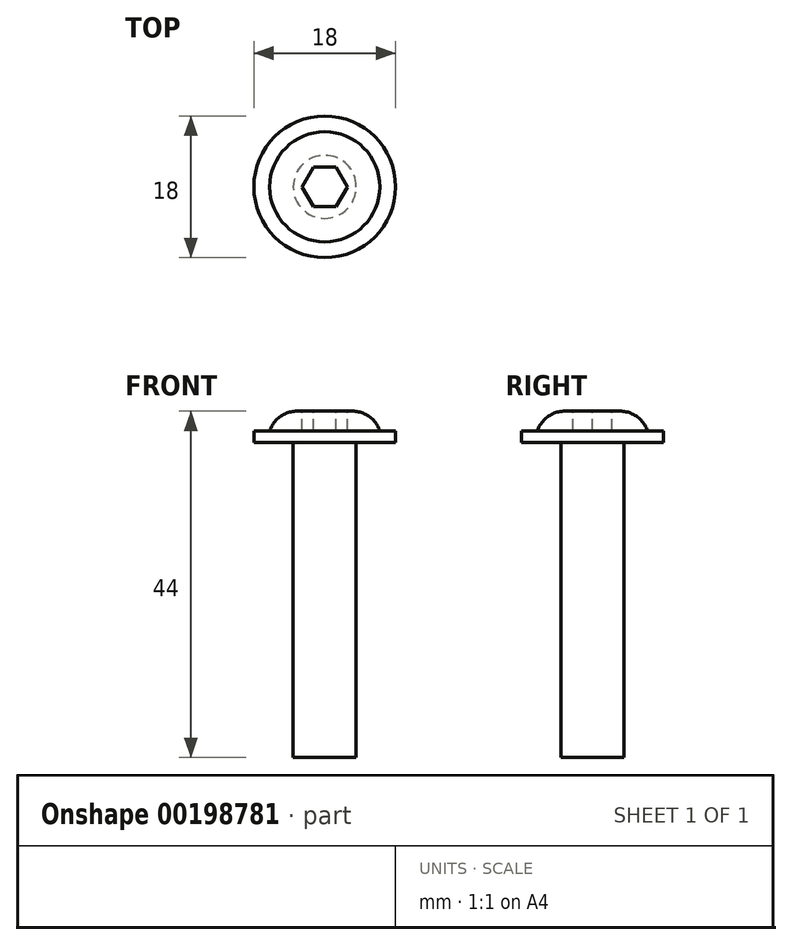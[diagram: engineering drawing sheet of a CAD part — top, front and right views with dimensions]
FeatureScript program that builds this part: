
annotation { "Feature Type Name" : "Feature", "Feature Type Description" : "" }
export const myFeature = defineFeature(function(context is Context, id is Id, definition is map)
    precondition{}
    {
        {
            var Q0;
            Q0=qCreatedBy(makeId("Front.planeOp"),FACE);
            var sketch = newSketch(context, id + "F0", { "sketchPlane" : qUnion([Q0])});
            skLineSegment(sketch, "E0", {"start": v(0, 0) * mm, "end": v(0, 44) * mm});
            skLineSegment(sketch, "E1", {"start": v(0, 44) * mm, "end": v(-3.5, 44) * mm});
            skLineSegment(sketch, "E2", {"start": v(0, 0) * mm, "end": v(-4, 0) * mm});
            skLineSegment(sketch, "E3", {"start": v(-4, 0) * mm, "end": v(-4, 40) * mm});
            skLineSegment(sketch, "E4", {"start": v(-4, 40) * mm, "end": v(-7, 40) * mm});
            skLineSegment(sketch, "E5", {"start": v(-7, 40) * mm, "end": v(-7, 41.5) * mm});
            skArc(sketch, "E6", {"start": v(-3.5, 44) * mm, "mid": v(-5.65, 43.31) * mm, "end": v(-7, 41.5) * mm});
            skSolve(sketch);
        }
        {
            var Q0;
            Q0=makeQuery(id+"F0.imprint","IMPRINT",FACE,{"disambiguationData":[TD([[makeQuery(id+"F0.imprint","IMPRINT",EDGE,{"derivedFrom":sQuery(id+"F0.wireOp",EDGE,"E0")}),1.0]])]});
            var Q1;
            Q1=sQuery(id+"F0.wireOp",EDGE,"E0");
            revolve(context, id + "F1", {"entities" : qUnion([Q0]), "axis" : qUnion([Q1]), "revolveType" : RevolveType.FULL});
        }
        {
            var Q0;
            Q0=makeQuery(id+"F1.opRevolve","SWEPT_FACE",FACE,{"disambiguationData":[OSD([sQuery(id+"F0.wireOp",EDGE,"E1")])]});
            var sketch = newSketch(context, id + "F2", { "sketchPlane" : qUnion([Q0])});
            skCircle(sketch, "E7.cCircle", {"center": v(0, 0) * mm, "radius": 2.5 * mm, "construction": true});
            skLineSegment(sketch, "E7.0", {"start": v(-1.44, 2.5) * mm, "end": v(1.44, 2.5) * mm});
            skLineSegment(sketch, "E7.1", {"start": v(1.44, 2.5) * mm, "end": v(2.89, 0) * mm});
            skLineSegment(sketch, "E7.2", {"start": v(2.89, 0) * mm, "end": v(1.44, -2.5) * mm});
            skLineSegment(sketch, "E7.3", {"start": v(1.44, -2.5) * mm, "end": v(-1.44, -2.5) * mm});
            skLineSegment(sketch, "E7.4", {"start": v(-1.44, -2.5) * mm, "end": v(-2.89, 0) * mm});
            skLineSegment(sketch, "E7.5", {"start": v(-2.89, 0) * mm, "end": v(-1.44, 2.5) * mm});
            skPoint(sketch, "E7.0.midPoint", {"position": v(0, 2.5) * mm});
            skSolve(sketch);
        }
        {
            var Q0;
            Q0 = qSketchRegion(id + "F2", true);
            extrude(context, id + "F3", {"entities" : qUnion([Q0]), "operationType" : NewBodyOperationType.REMOVE, "oppositeDirection" : true, "depth" : 3 * mm});
        }
        {
            var Q0;
            Q0=makeQuery(id+"F1.opRevolve","SWEPT_FACE",FACE,{"disambiguationData":[OSD([sQuery(id+"F0.wireOp",EDGE,"E4")])]});
            var sketch = newSketch(context, id + "F4", { "sketchPlane" : qUnion([Q0])});
            skCircle(sketch, "E8", {"center": v(0, 0) * mm, "radius": 9 * mm});
            skSolve(sketch);
        }
        {
            var Q0;
            Q0 = qSketchRegion(id + "F4", true);
            extrude(context, id + "F5", {"entities" : qUnion([Q0]), "operationType" : NewBodyOperationType.ADD, "oppositeDirection" : true, "depth" : 1.5 * mm});
        }
    });
